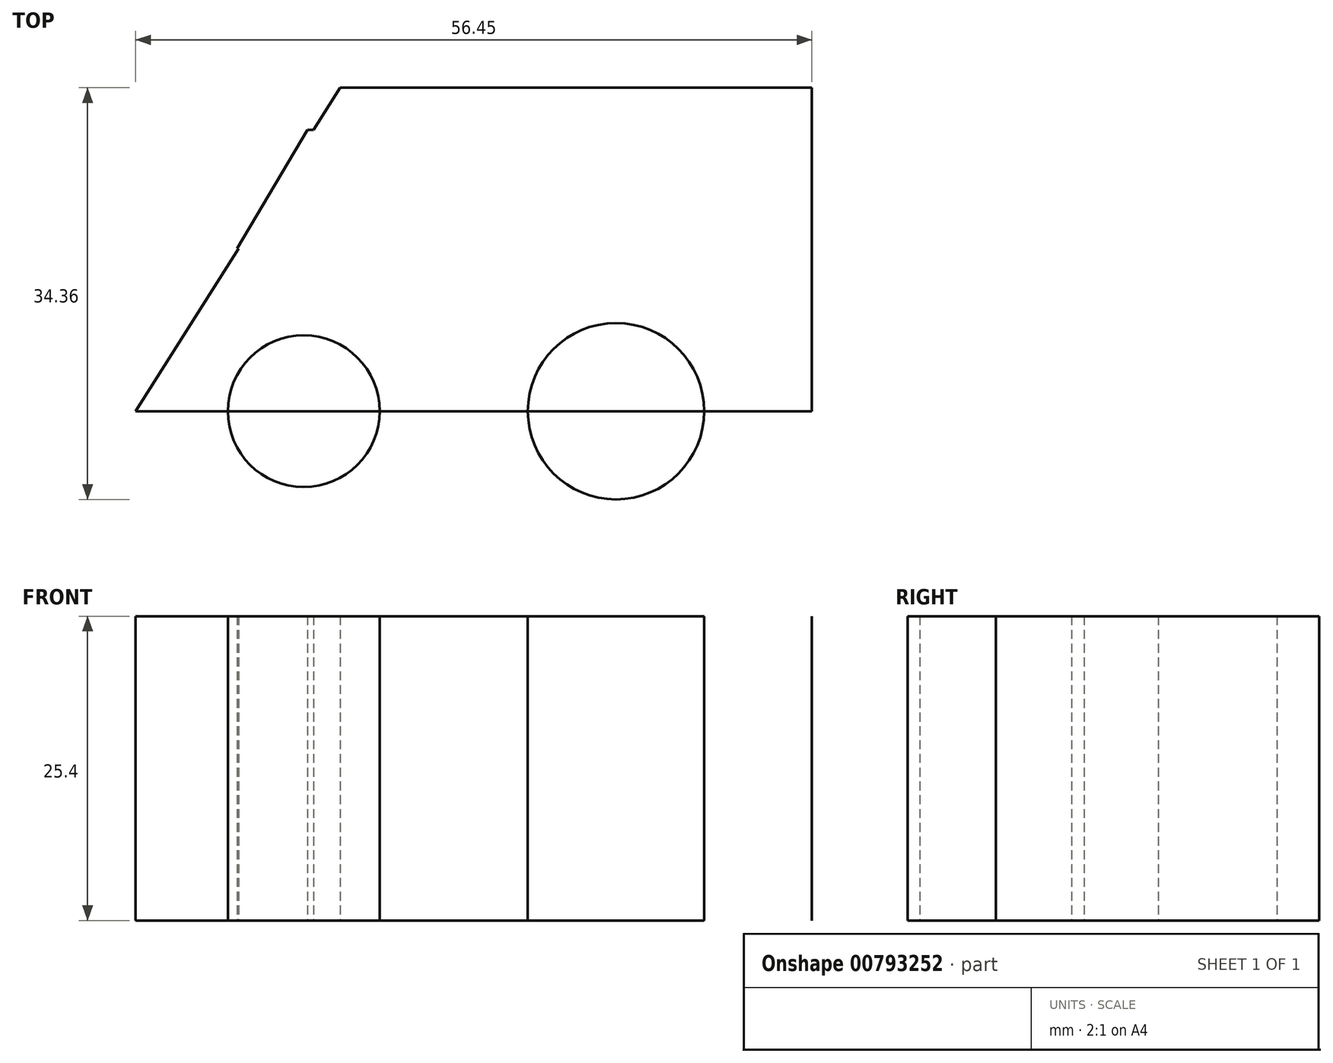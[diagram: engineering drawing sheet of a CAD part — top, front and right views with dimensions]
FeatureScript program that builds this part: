
annotation { "Feature Type Name" : "Feature", "Feature Type Description" : "" }
export const myFeature = defineFeature(function(context is Context, id is Id, definition is map)
    precondition{}
    {
        {
            var Q0;
            Q0=qCreatedBy(makeId("Top.planeOp"),FACE);
            var sketch = newSketch(context, id + "F0", { "sketchPlane" : qUnion([Q0])});
            skLineSegment(sketch, "E0", {"start": v(-25.8, 0) * mm, "end": v(30.9, 0) * mm});
            skLineSegment(sketch, "E1", {"start": v(30.9, 0) * mm, "end": v(30.9, 27.7) * mm});
            skLineSegment(sketch, "E2", {"start": v(30.9, 27.7) * mm, "end": v(-8.85, 27.7) * mm});
            skLineSegment(sketch, "E3", {"start": v(-8.85, 27.7) * mm, "end": v(-25.8, 0) * mm});
            skCircle(sketch, "E4", {"center": v(-11.72, 0) * mm, "radius": 6.33 * mm});
            skCircle(sketch, "E5", {"center": v(14.35, 0) * mm, "radius": 7.36 * mm});
            skSolve(sketch);
        }
        {
            var Q0;
            {var subQ0=sQuery(id+"F0.wireOp",EDGE,"E1");Q0=makeQuery(id+"F0.imprint","IMPRINT",FACE,{"disambiguationData":[TD([[makeQuery(id+"F0.imprint","IMPRINT",EDGE,{"derivedFrom":subQ0}),1.0]])]});}
            var sketch = newSketch(context, id + "F1", { "sketchPlane" : qUnion([Q0])});
            skSolve(sketch);
        }
        {
            var Q0;
            Q0 = qSketchRegion(id + "F1", true);
            var Q1;
            {var subQ0=sQuery(id+"F0.wireOp",EDGE,"E4");var subQ1=sQuery(id+"F0.wireOp",EDGE,"E0");var subQ2=makeQuery(id+"F0.imprint","INTERSECT",VERTEX,{"disambiguationData":[OD(0.0)],"derivedFrom":[subQ1,subQ0]});Q1=makeQuery(id+"F0.imprint","IMPRINT",FACE,{"disambiguationData":[TD([[makeQuery(id+"F0.imprint","IMPRINT",EDGE,{"disambiguationData":[TD([[subQ2,-1.0]])],"derivedFrom":subQ1}),-1.0]])]});}
            var Q2;
            {var subQ0=sQuery(id+"F0.wireOp",EDGE,"E5");var subQ1=sQuery(id+"F0.wireOp",EDGE,"E0");var subQ2=makeQuery(id+"F0.imprint","INTERSECT",VERTEX,{"disambiguationData":[OD(0.0)],"derivedFrom":[subQ1,subQ0]});Q2=makeQuery(id+"F0.imprint","IMPRINT",FACE,{"disambiguationData":[TD([[makeQuery(id+"F0.imprint","IMPRINT",EDGE,{"disambiguationData":[TD([[subQ2,-1.0]])],"derivedFrom":subQ1}),1.0]])]});}
            var Q3;
            {var subQ0=sQuery(id+"F0.wireOp",EDGE,"E4");var subQ1=sQuery(id+"F0.wireOp",EDGE,"E0");var subQ2=makeQuery(id+"F0.imprint","INTERSECT",VERTEX,{"disambiguationData":[OD(0.0)],"derivedFrom":[subQ1,subQ0]});Q3=makeQuery(id+"F0.imprint","IMPRINT",FACE,{"disambiguationData":[TD([[makeQuery(id+"F0.imprint","IMPRINT",EDGE,{"disambiguationData":[TD([[subQ2,-1.0]])],"derivedFrom":subQ1}),1.0]])]});}
            var Q4;
            {var subQ0=sQuery(id+"F0.wireOp",EDGE,"E5");var subQ1=sQuery(id+"F0.wireOp",EDGE,"E0");var subQ2=makeQuery(id+"F0.imprint","INTERSECT",VERTEX,{"disambiguationData":[OD(0.0)],"derivedFrom":[subQ1,subQ0]});Q4=makeQuery(id+"F0.imprint","IMPRINT",FACE,{"disambiguationData":[TD([[makeQuery(id+"F0.imprint","IMPRINT",EDGE,{"disambiguationData":[TD([[subQ2,-1.0]])],"derivedFrom":subQ1}),-1.0]])]});}
            extrude(context, id + "F2", {"entities" : qUnion([Q0, Q1, Q2, Q3, Q4]), "depth" : 25.4 * mm, "offsetDistance" : 25.4 * mm});
        }
        {
            var Q0;
            {var subQ0=sQuery(id+"F0.wireOp",EDGE,"E1");Q0=makeQuery(id+"F1.imprint","IMPRINT",FACE,{"disambiguationData":[TD([[makeQuery(id+"F1.imprint","IMPRINT",EDGE,{"derivedFrom":makeQuery(id+"F0.imprint","IMPRINT",EDGE,{"derivedFrom":subQ0})}),1.0]])]});}
            var sketch = newSketch(context, id + "F3", { "sketchPlane" : qUnion([Q0])});
            skLineSegment(sketch, "E6", {"start": v(-6.59, 13.57) * mm, "end": v(-6.59, 23.48) * mm});
            skLineSegment(sketch, "E7", {"start": v(-6.59, 23.48) * mm, "end": v(-11.4, 23.48) * mm});
            skLineSegment(sketch, "E8", {"start": v(-6.59, 13.57) * mm, "end": v(-17.28, 13.57) * mm});
            skLineSegment(sketch, "E9", {"start": v(-17.28, 13.57) * mm, "end": v(-11.4, 23.48) * mm});
            skLineSegment(sketch, "E10", {"start": v(-25.75, 0) * mm, "end": v(-8.67, 27) * mm});
            skLineSegment(sketch, "E11", {"start": v(-8.67, 27) * mm, "end": v(30.7, 27) * mm});
            skLineSegment(sketch, "E12", {"start": v(30.7, 27) * mm, "end": v(30.7, 0) * mm});
            skLineSegment(sketch, "E13", {"start": v(30.7, 0) * mm, "end": v(-25.75, 0) * mm});
            skSolve(sketch);
        }
        {
            var Q0;
            Q0 = qSketchRegion(id + "F3", true);
            extrude(context, id + "F4", {"entities" : qUnion([Q0]), "depth" : 25.4 * mm, "offsetDistance" : 25.4 * mm});
        }
    });
